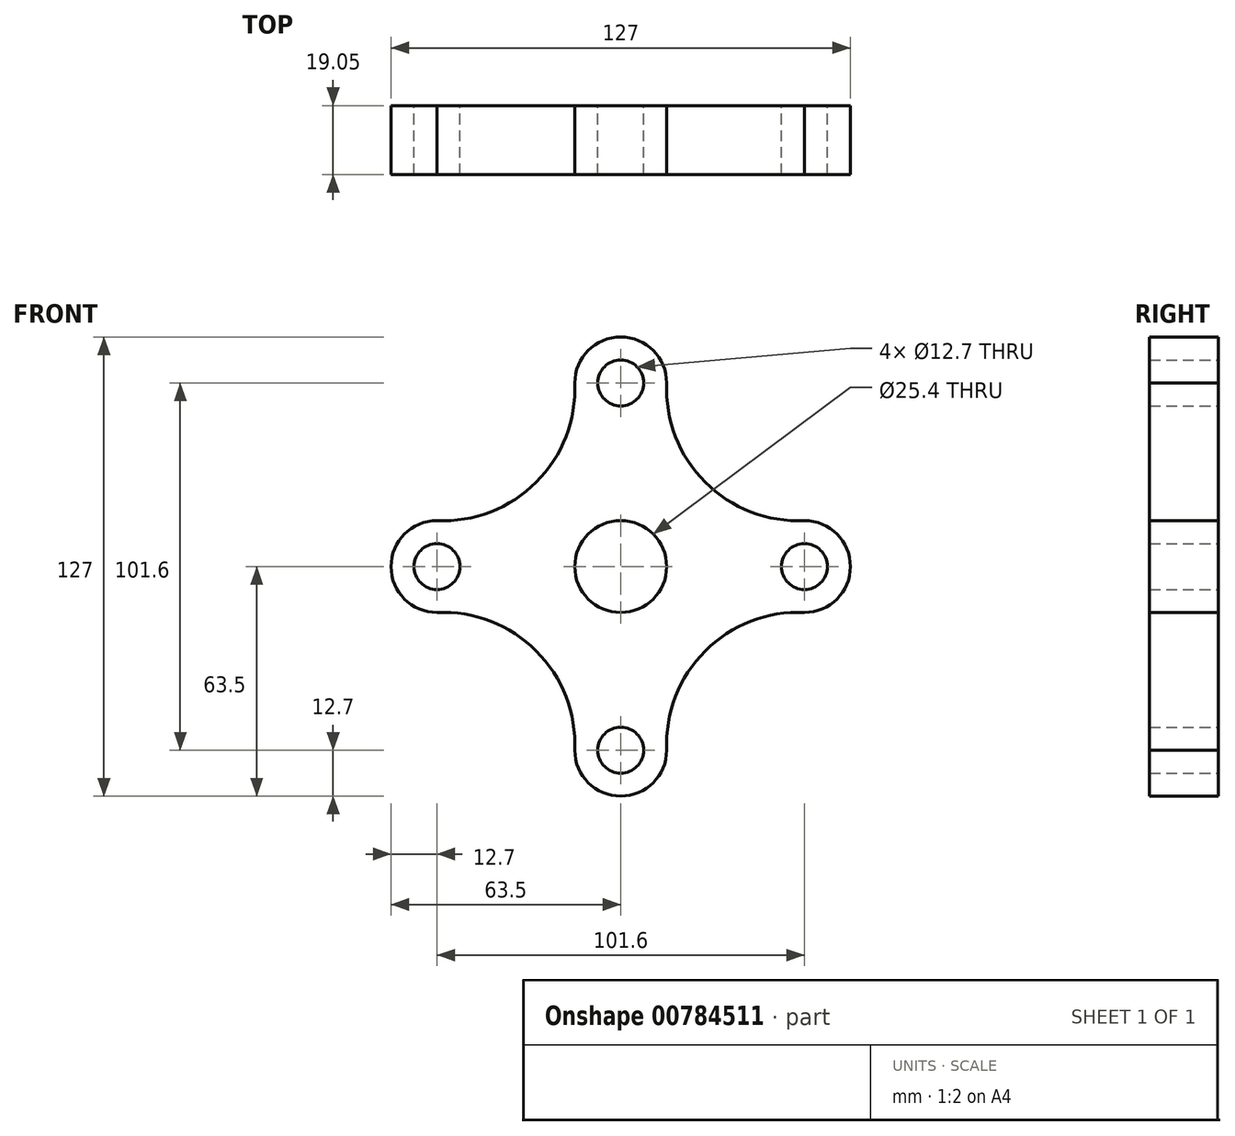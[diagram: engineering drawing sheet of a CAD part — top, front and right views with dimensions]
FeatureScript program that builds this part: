
annotation { "Feature Type Name" : "Feature", "Feature Type Description" : "" }
export const myFeature = defineFeature(function(context is Context, id is Id, definition is map)
    precondition{}
    {
        {
            var Q0;
            Q0=qCreatedBy(makeId("Front.planeOp"),FACE);
            var sketch = newSketch(context, id + "F0", { "sketchPlane" : qUnion([Q0])});
            skCircle(sketch, "E0", {"center": v(0, 0) * mm, "radius": 12.7 * mm});
            skCircle(sketch, "E1", {"center": v(0, -50.8) * mm, "radius": 6.35 * mm});
            skCircle(sketch, "E2", {"center": v(-50.8, 0) * mm, "radius": 6.35 * mm});
            skCircle(sketch, "E3", {"center": v(0, 50.8) * mm, "radius": 6.35 * mm});
            skCircle(sketch, "E4", {"center": v(50.8, 0) * mm, "radius": 6.35 * mm});
            skLineSegment(sketch, "E5", {"start": v(0, 50.8) * mm, "end": v(0, 12.7) * mm});
            skLineSegment(sketch, "E6", {"start": v(-50.8, 0) * mm, "end": v(-44.45, 0) * mm});
            skLineSegment(sketch, "E7", {"start": v(0, -50.8) * mm, "end": v(0, -12.7) * mm});
            skLineSegment(sketch, "E8", {"start": v(44.45, 0) * mm, "end": v(50.8, 0) * mm});
            skLineSegment(sketch, "E9", {"start": v(0, -50.8) * mm, "end": v(-6.35, -50.8) * mm});
            skLineSegment(sketch, "E10", {"start": v(0, 50.8) * mm, "end": v(6.35, 50.8) * mm});
            skLineSegment(sketch, "E11", {"start": v(0, 50.8) * mm, "end": v(-6.35, 50.8) * mm});
            skArc(sketch, "E12", {"start": v(-50.8, 12.7) * mm, "mid": v(-23.36, 23.36) * mm, "end": v(-12.7, 50.8) * mm});
            skArc(sketch, "E13", {"start": v(-12.7, -50.8) * mm, "mid": v(-23.36, -23.36) * mm, "end": v(-50.8, -12.7) * mm});
            skArc(sketch, "E14", {"start": v(50.8, -12.7) * mm, "mid": v(23.36, -23.36) * mm, "end": v(12.7, -50.8) * mm});
            skArc(sketch, "E15", {"start": v(12.7, 50.8) * mm, "mid": v(23.36, 23.36) * mm, "end": v(50.8, 12.7) * mm});
            skArc(sketch, "E16", {"start": v(-50.8, 12.7) * mm, "mid": v(-63.5, 0) * mm, "end": v(-50.8, -12.7) * mm});
            skArc(sketch, "E17", {"start": v(-12.7, -50.8) * mm, "mid": v(0, -63.5) * mm, "end": v(12.7, -50.8) * mm});
            skArc(sketch, "E18", {"start": v(50.8, -12.7) * mm, "mid": v(63.5, 0) * mm, "end": v(50.8, 12.7) * mm});
            skArc(sketch, "E19", {"start": v(12.7, 50.8) * mm, "mid": v(0, 63.5) * mm, "end": v(-12.7, 50.8) * mm});
            skSolve(sketch);
        }
        {
            var Q0;
            Q0 = qSketchRegion(id + "F0", true);
            extrude(context, id + "F1", {"entities" : qUnion([Q0]), "depth" : 19.05 * mm, "offsetDistance" : 25.4 * mm});
        }
    });
